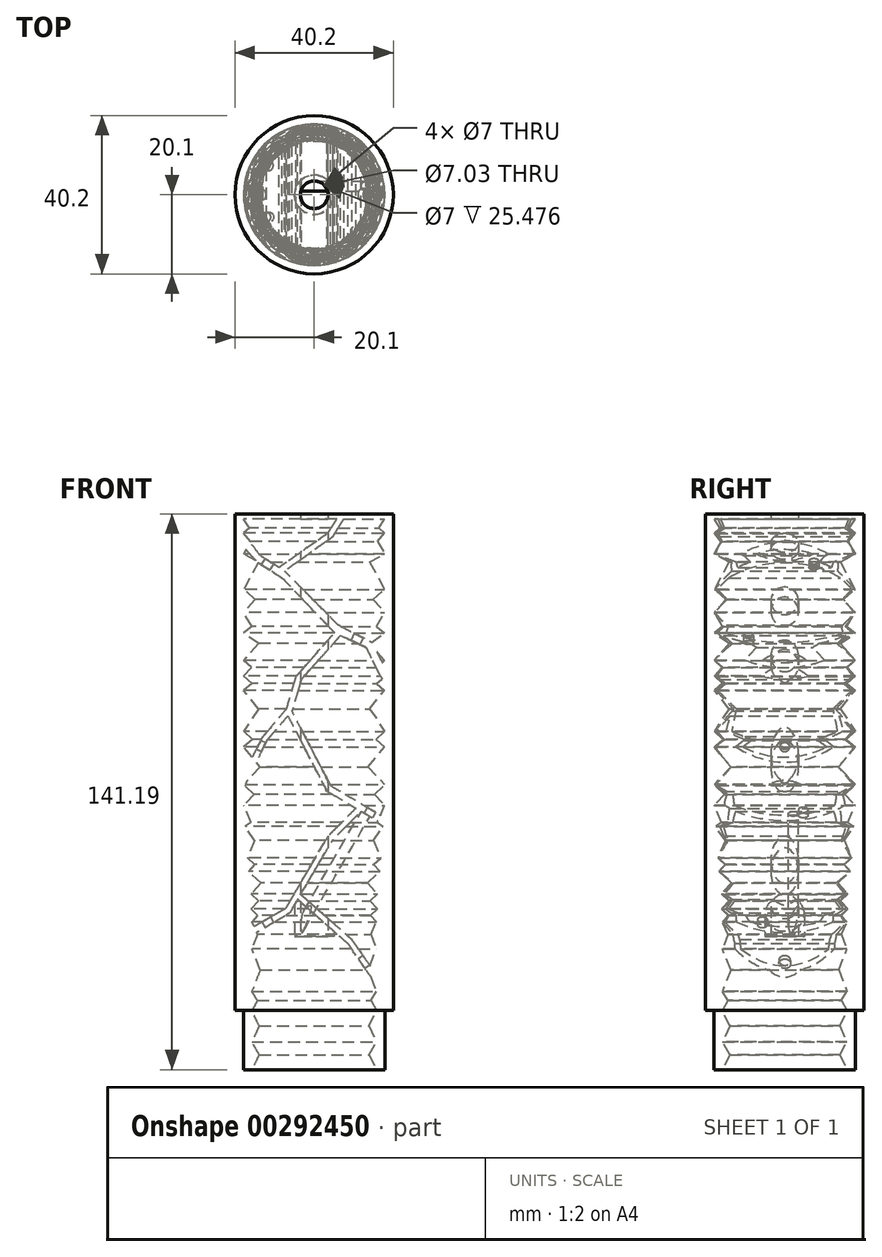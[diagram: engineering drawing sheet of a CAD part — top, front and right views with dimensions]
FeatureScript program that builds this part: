
annotation { "Feature Type Name" : "Feature", "Feature Type Description" : "" }
export const myFeature = defineFeature(function(context is Context, id is Id, definition is map)
    precondition{}
    {
        {
            var Q0;
            Q0=qCreatedBy(makeId("Front.planeOp"),FACE);
            var sketch = newSketch(context, id + "F0", { "sketchPlane" : qUnion([Q0])});
            skLineSegment(sketch, "E0", {"start": v(0, 0) * mm, "end": v(0, 175) * mm, "construction": true});
            skLineSegment(sketch, "E1", {"start": v(-3, 0) * mm, "end": v(-3, 175) * mm, "construction": true});
            skLineSegment(sketch, "E2", {"start": v(-3.5, -0.01) * mm, "end": v(-3.5, 175) * mm, "construction": true});
            skLineSegment(sketch, "E3", {"start": v(-9.9, 0) * mm, "end": v(-9.9, 175) * mm, "construction": true});
            skLineSegment(sketch, "E4", {"start": v(-20, 0) * mm, "end": v(-20, 175) * mm, "construction": true});
            skLineSegment(sketch, "E5", {"start": v(4.04, 175) * mm, "end": v(-22.22, 175) * mm, "construction": true});
            skLineSegment(sketch, "E6", {"start": v(23.08, 173.82) * mm, "end": v(-22.24, 173.82) * mm, "construction": true});
            skLineSegment(sketch, "E7", {"start": v(-17.94, 0) * mm, "end": v(-17.94, 175) * mm, "construction": true});
            skLineSegment(sketch, "E8", {"start": v(-22.12, 25) * mm, "end": v(22.75, 25) * mm, "construction": true});
            skLineSegment(sketch, "E9.MirrorCS", {"start": v(3, 0) * mm, "end": v(3, 175) * mm, "construction": true});
            skLineSegment(sketch, "E10.MirrorCS", {"start": v(17.94, 0) * mm, "end": v(17.94, 175) * mm, "construction": true});
            skLineSegment(sketch, "E11.MirrorCS", {"start": v(20, 0) * mm, "end": v(20, 175) * mm, "construction": true});
            skLineSegment(sketch, "E12.MirrorCS", {"start": v(9.9, 0) * mm, "end": v(9.9, 175) * mm, "construction": true});
            skLineSegment(sketch, "E13.MirrorCS", {"start": v(3.5, -0.01) * mm, "end": v(3.5, 175) * mm, "construction": true});
            skSolve(sketch);
        }
        {
            var Q0;
            Q0=qCreatedBy(makeId("Front.planeOp"),FACE);
            var sketch = newSketch(context, id + "F1", { "sketchPlane" : qUnion([Q0])});
            skLineSegment(sketch, "E14", {"start": v(-18.18, 170.36) * mm, "end": v(-13.69, 164.42) * mm});
            skLineSegment(sketch, "E15", {"start": v(-7.52, 160.5) * mm, "end": v(6.1, 146.8) * mm});
            skLineSegment(sketch, "E16", {"start": v(6.1, 146.8) * mm, "end": v(14.83, 142.3) * mm});
            skLineSegment(sketch, "E17", {"start": v(14.83, 142.3) * mm, "end": v(18.14, 135.62) * mm});
            skLineSegment(sketch, "E18", {"start": v(-18.18, 166.91) * mm, "end": v(-14.47, 162.75) * mm});
            skLineSegment(sketch, "E19", {"start": v(-14.47, 162.75) * mm, "end": v(-8.16, 158.78) * mm});
            skLineSegment(sketch, "E20", {"start": v(-8.16, 158.78) * mm, "end": v(5.17, 144.84) * mm});
            skLineSegment(sketch, "E21", {"start": v(13.17, 141.1) * mm, "end": v(18.14, 131.23) * mm});
            skLineSegment(sketch, "E22", {"start": v(5.17, 144.84) * mm, "end": v(-4.56, 133.73) * mm});
            skLineSegment(sketch, "E23", {"start": v(-4.56, 133.73) * mm, "end": v(-7, 125.56) * mm});
            skLineSegment(sketch, "E24", {"start": v(-7, 125.56) * mm, "end": v(-13, 118.44) * mm});
            skLineSegment(sketch, "E25", {"start": v(-13, 118.44) * mm, "end": v(-18.1, 108.79) * mm});
            skLineSegment(sketch, "E26", {"start": v(6.7, 144.13) * mm, "end": v(-3.27, 132.97) * mm});
            skLineSegment(sketch, "E27", {"start": v(-3.27, 132.97) * mm, "end": v(-5.65, 124.9) * mm});
            skLineSegment(sketch, "E28", {"start": v(-12.05, 117.46) * mm, "end": v(-18.18, 104.65) * mm});
            skLineSegment(sketch, "E29", {"start": v(-5.65, 124.9) * mm, "end": v(4.16, 105.99) * mm});
            skLineSegment(sketch, "E30", {"start": v(4.16, 105.99) * mm, "end": v(18.19, 97.67) * mm});
            skLineSegment(sketch, "E31", {"start": v(-6.67, 123.72) * mm, "end": v(3.26, 104.57) * mm});
            skLineSegment(sketch, "E32", {"start": v(11.94, 99.46) * mm, "end": v(4.73, 92.25) * mm});
            skLineSegment(sketch, "E33", {"start": v(-6.2, 73.65) * mm, "end": v(-18.06, 66.64) * mm});
            skLineSegment(sketch, "E34", {"start": v(10.6, 100.25) * mm, "end": v(3.57, 93.2) * mm});
            skLineSegment(sketch, "E35", {"start": v(3.57, 93.2) * mm, "end": v(-7.24, 74.85) * mm});
            skLineSegment(sketch, "E36", {"start": v(-7.24, 74.85) * mm, "end": v(-18.1, 68.51) * mm});
            skLineSegment(sketch, "E37", {"start": v(-7.52, 160.5) * mm, "end": v(4.81, 169.32) * mm});
            skLineSegment(sketch, "E38", {"start": v(4.81, 169.32) * mm, "end": v(7.67, 174.04) * mm});
            skLineSegment(sketch, "E39", {"start": v(-8.95, 161.41) * mm, "end": v(3.46, 170.08) * mm});
            skLineSegment(sketch, "E40", {"start": v(3.46, 170.08) * mm, "end": v(5.98, 174.08) * mm});
            skLineSegment(sketch, "E41", {"start": v(-4.19, 77.08) * mm, "end": v(8.56, 65.84) * mm});
            skLineSegment(sketch, "E42", {"start": v(8.56, 65.84) * mm, "end": v(18.14, 51.86) * mm});
            skLineSegment(sketch, "E43", {"start": v(-3.44, 78.36) * mm, "end": v(9.57, 66.88) * mm});
            skLineSegment(sketch, "E44", {"start": v(9.57, 66.88) * mm, "end": v(18.14, 54.47) * mm});
            skLineSegment(sketch, "E45", {"start": v(-13.69, 164.42) * mm, "end": v(-8.95, 161.41) * mm});
            skLineSegment(sketch, "E46", {"start": v(-18.18, 170.36) * mm, "end": v(-18.18, 166.91) * mm});
            skLineSegment(sketch, "E47", {"start": v(13.17, 141.1) * mm, "end": v(6.7, 144.13) * mm});
            skLineSegment(sketch, "E48", {"start": v(18.14, 135.62) * mm, "end": v(18.14, 131.23) * mm});
            skLineSegment(sketch, "E49", {"start": v(-12.05, 117.46) * mm, "end": v(-6.67, 123.72) * mm});
            skLineSegment(sketch, "E50", {"start": v(18.19, 97.67) * mm, "end": v(18.19, 95.85) * mm});
            skLineSegment(sketch, "E51", {"start": v(18.19, 95.85) * mm, "end": v(11.94, 99.46) * mm});
            skLineSegment(sketch, "E52", {"start": v(10.6, 100.25) * mm, "end": v(3.26, 104.57) * mm});
            skLineSegment(sketch, "E53", {"start": v(4.73, 92.25) * mm, "end": v(-3.44, 78.36) * mm});
            skLineSegment(sketch, "E54", {"start": v(-4.19, 77.08) * mm, "end": v(-6.2, 73.65) * mm});
            skLineSegment(sketch, "E55", {"start": v(-18.1, 68.51) * mm, "end": v(-18.06, 66.64) * mm});
            skLineSegment(sketch, "E56", {"start": v(18.14, 54.47) * mm, "end": v(18.14, 51.86) * mm});
            skLineSegment(sketch, "E57", {"start": v(5.98, 174.08) * mm, "end": v(7.67, 174.04) * mm});
            skLineSegment(sketch, "E58", {"start": v(-18.1, 108.79) * mm, "end": v(-18.18, 104.65) * mm});
            skSolve(sketch);
        }
        {
            var Q0;
            Q0=qSketchRegion(id+"F1",true);
            extrude(context, id + "F2", {"entities" : qUnion([Q0]), "depth" : 25 * mm, "hasSecondDirection" : true, "secondDirectionOppositeDirection" : true, "secondDirectionDepth" : 25 * mm});
        }
        {
            var Q0;
            Q0=qCreatedBy(makeId("Front.planeOp"),FACE);
            var sketch = newSketch(context, id + "F3", { "sketchPlane" : qUnion([Q0])});
            skLineSegment(sketch, "E59", {"start": v(17.93, 175.1) * mm, "end": v(17.93, -3.26) * mm});
            skLineSegment(sketch, "E60", {"start": v(17.93, -3.26) * mm, "end": v(50.8, -3.26) * mm});
            skLineSegment(sketch, "E61", {"start": v(50.8, -3.26) * mm, "end": v(50.8, 174.97) * mm});
            skLineSegment(sketch, "E62", {"start": v(50.8, 174.97) * mm, "end": v(17.93, 175.1) * mm});
            skSolve(sketch);
        }
        {
            var Q0;
            Q0=qSketchRegion(id+"F3",true);
            var Q1;
            Q1=sQuery(id+"F0.wireOp",EDGE,"E0");
            revolve(context, id + "F4", {"operationType" : NewBodyOperationType.REMOVE, "entities" : qUnion([Q0]), "axis" : qUnion([Q1]), "revolveType" : RevolveType.FULL, "oppositeDirection" : true});
        }
        {
            var Q0;
            Q0=qCreatedBy(makeId("Front.planeOp"),FACE);
            var sketch = newSketch(context, id + "F5", { "sketchPlane" : qUnion([Q0])});
            skLineSegment(sketch, "E63", {"start": v(-17.9, 173.79) * mm, "end": v(-3.52, 173.79) * mm});
            skLineSegment(sketch, "E64", {"start": v(-3.52, 173.79) * mm, "end": v(-3.52, 175) * mm});
            skLineSegment(sketch, "E65", {"start": v(-3.52, 175) * mm, "end": v(-20.1, 174.99) * mm});
            skLineSegment(sketch, "E66", {"start": v(0, 0) * mm, "end": v(0, 25.6) * mm, "construction": true});
            skLineSegment(sketch, "E67", {"start": v(-17.97, 59.66) * mm, "end": v(-17.97, 0) * mm, "construction": true});
            skLineSegment(sketch, "E68", {"start": v(-13.16, 33.82) * mm, "end": v(-23.02, 33.82) * mm, "construction": true});
            skLineSegment(sketch, "E69", {"start": v(-12.48, 48.82) * mm, "end": v(-23.12, 48.82) * mm, "construction": true});
            skLineSegment(sketch, "E70", {"start": v(-20.1, 48.82) * mm, "end": v(-17.97, 48.82) * mm});
            skLineSegment(sketch, "E71", {"start": v(-17.97, 48.82) * mm, "end": v(-17.97, 33.82) * mm});
            skLineSegment(sketch, "E72", {"start": v(-17.97, 33.82) * mm, "end": v(-15.82, 33.82) * mm});
            skLineSegment(sketch, "E73", {"start": v(-20.1, 48.82) * mm, "end": v(-20.1, 174.99) * mm});
            skLineSegment(sketch, "E74", {"start": v(-15.82, 33.82) * mm, "end": v(-13.98, 37.62) * mm});
            skLineSegment(sketch, "E75", {"start": v(-13.98, 37.62) * mm, "end": v(-15.82, 40.87) * mm});
            skLineSegment(sketch, "E76", {"start": v(-15.82, 40.87) * mm, "end": v(-13.98, 44.9) * mm});
            skLineSegment(sketch, "E77", {"start": v(-13.98, 44.9) * mm, "end": v(-15.82, 48.82) * mm});
            skLineSegment(sketch, "E78", {"start": v(-15.82, 48.82) * mm, "end": v(-14.42, 51.4) * mm});
            skLineSegment(sketch, "E79", {"start": v(-14.42, 51.4) * mm, "end": v(-15.82, 53.68) * mm});
            skLineSegment(sketch, "E80", {"start": v(-15.82, 53.68) * mm, "end": v(-13.71, 59.11) * mm});
            skLineSegment(sketch, "E81", {"start": v(-13.71, 59.11) * mm, "end": v(-15.82, 64.55) * mm});
            skLineSegment(sketch, "E82", {"start": v(-15.82, 64.55) * mm, "end": v(-14.42, 68.24) * mm});
            skLineSegment(sketch, "E83", {"start": v(-14.42, 68.24) * mm, "end": v(-15.82, 71.42) * mm});
            skLineSegment(sketch, "E84", {"start": v(-15.82, 71.42) * mm, "end": v(-14.33, 73.06) * mm});
            skLineSegment(sketch, "E85", {"start": v(-14.33, 73.06) * mm, "end": v(-16.05, 74.62) * mm});
            skLineSegment(sketch, "E86", {"start": v(-16.05, 74.62) * mm, "end": v(-14.14, 76.73) * mm});
            skLineSegment(sketch, "E87", {"start": v(-14.14, 76.73) * mm, "end": v(-16.05, 78.46) * mm});
            skLineSegment(sketch, "E88", {"start": v(-16.05, 78.46) * mm, "end": v(-13.5, 81.26) * mm});
            skLineSegment(sketch, "E89", {"start": v(-13.5, 81.26) * mm, "end": v(-16.72, 84.18) * mm});
            skLineSegment(sketch, "E90", {"start": v(-16.72, 84.18) * mm, "end": v(-15.11, 85.95) * mm});
            skLineSegment(sketch, "E91", {"start": v(-15.11, 85.95) * mm, "end": v(-16.96, 87.62) * mm});
            skLineSegment(sketch, "E92", {"start": v(-16.96, 87.62) * mm, "end": v(-15.11, 92.02) * mm});
            skLineSegment(sketch, "E93", {"start": v(-15.11, 92.02) * mm, "end": v(-17.53, 95.61) * mm});
            skLineSegment(sketch, "E94", {"start": v(-17.53, 95.61) * mm, "end": v(-16.05, 96.6) * mm});
            skLineSegment(sketch, "E95", {"start": v(-16.05, 96.6) * mm, "end": v(-17.9, 100.99) * mm});
            skLineSegment(sketch, "E96", {"start": v(-17.9, 100.99) * mm, "end": v(-15.29, 103.78) * mm});
            skLineSegment(sketch, "E97", {"start": v(-15.29, 103.78) * mm, "end": v(-17.9, 106.24) * mm});
            skLineSegment(sketch, "E98", {"start": v(-17.9, 106.24) * mm, "end": v(-13.7, 110.72) * mm});
            skLineSegment(sketch, "E99", {"start": v(-13.7, 110.72) * mm, "end": v(-17.9, 115.82) * mm});
            skLineSegment(sketch, "E100", {"start": v(-17.9, 115.82) * mm, "end": v(-15.67, 117.66) * mm});
            skLineSegment(sketch, "E101", {"start": v(-15.67, 117.66) * mm, "end": v(-17.9, 119.8) * mm});
            skLineSegment(sketch, "E102", {"start": v(-17.9, 119.8) * mm, "end": v(-14.11, 125.5) * mm});
            skLineSegment(sketch, "E103", {"start": v(-14.11, 125.5) * mm, "end": v(-17.9, 130.2) * mm});
            skLineSegment(sketch, "E104", {"start": v(-17.9, 130.2) * mm, "end": v(-15.8, 131.9) * mm});
            skLineSegment(sketch, "E105", {"start": v(-15.8, 131.9) * mm, "end": v(-17.9, 133.78) * mm});
            skLineSegment(sketch, "E106", {"start": v(-17.9, 133.78) * mm, "end": v(-15.88, 136.02) * mm});
            skLineSegment(sketch, "E107", {"start": v(-15.88, 136.02) * mm, "end": v(-17.9, 137.85) * mm});
            skLineSegment(sketch, "E108", {"start": v(-17.9, 137.85) * mm, "end": v(-14.11, 142.04) * mm});
            skLineSegment(sketch, "E109", {"start": v(-14.11, 142.04) * mm, "end": v(-17.9, 144.8) * mm});
            skLineSegment(sketch, "E110", {"start": v(-17.9, 144.8) * mm, "end": v(-15.82, 146.48) * mm});
            skLineSegment(sketch, "E111", {"start": v(-15.82, 146.48) * mm, "end": v(-17.9, 149.93) * mm});
            skLineSegment(sketch, "E112", {"start": v(-17.9, 149.93) * mm, "end": v(-14.97, 153.33) * mm});
            skLineSegment(sketch, "E113", {"start": v(-14.97, 153.33) * mm, "end": v(-17.9, 155.86) * mm});
            skLineSegment(sketch, "E114", {"start": v(-17.9, 155.86) * mm, "end": v(-14.11, 162.77) * mm});
            skLineSegment(sketch, "E115", {"start": v(-14.11, 162.77) * mm, "end": v(-17.9, 164.85) * mm});
            skLineSegment(sketch, "E116", {"start": v(-17.9, 164.85) * mm, "end": v(-16.15, 168.05) * mm});
            skLineSegment(sketch, "E117", {"start": v(-16.15, 168.05) * mm, "end": v(-17.9, 170.23) * mm});
            skLineSegment(sketch, "E118", {"start": v(-17.9, 170.23) * mm, "end": v(-16.44, 171.41) * mm});
            skLineSegment(sketch, "E119", {"start": v(-16.44, 171.41) * mm, "end": v(-17.9, 173.79) * mm});
            skSolve(sketch);
        }
        {
            var Q0;
            Q0=qSketchRegion(id+"F5",true);
            var Q1;
            Q1=sQuery(id+"F5.wireOp",EDGE,"E66");
            revolve(context, id + "F6", {"operationType" : NewBodyOperationType.ADD, "entities" : qUnion([Q0]), "axis" : qUnion([Q1]), "revolveType" : RevolveType.FULL});
        }
        {
            var Q0;
            Q0=qCreatedBy(makeId("Top.planeOp"),FACE);
            var sketch = newSketch(context, id + "F7", { "sketchPlane" : qUnion([Q0])});
            skCircle(sketch, "E120", {"center": v(0, 0) * mm, "radius": 3.5 * mm});
            skSolve(sketch);
        }
        {
            var Q0;
            Q0=qSketchRegion(id+"F7",true);
            extrude(context, id + "F8", {"entities" : qUnion([Q0]), "operationType" : NewBodyOperationType.REMOVE, "endBound" : BoundingType.THROUGH_ALL, "depth" : 25 * mm});
        }
        {
            var Q0;
            Q0=qCreatedBy(makeId("Top.planeOp"),FACE);
            cPlane(context, id + "F9", {"entities" : qUnion([Q0]), "cplaneType" : CPlaneType.OFFSET, "offset" : 67.7 * mm, "width" : 150 * mm, "height" : 150 * mm});
        }
        {
            var Q0;
            Q0=qCreatedBy(id+"F9.planeOp",FACE);
            var sketch = newSketch(context, id + "F10", { "sketchPlane" : qUnion([Q0])});
            skCircle(sketch, "E121", {"center": v(0, 0) * mm, "radius": 3.5 * mm});
            skCircle(sketch, "E122", {"center": v(0, 0) * mm, "radius": 5 * mm});
            skSolve(sketch);
        }
        {
            var Q0;
            Q0=qSketchRegion(id+"F10",true);
            var Q1;
            Q1=makeQuery(id+"F2.opExtrude","SWEPT_FACE",FACE,{"disambiguationData":[OSD([sQuery(id+"F1.wireOp",EDGE,"E41")])]});
            extrude(context, id + "F11", {"entities" : qUnion([Q0]), "operationType" : NewBodyOperationType.ADD, "endBound" : BoundingType.UP_TO_SURFACE, "endBoundEntityFace" : qUnion([Q1]), "depth" : 25 * mm});
        }
        {
            var Q0;
            Q0=makeQuery(id+"F2.opExtrude","SWEPT_FACE",FACE,{"disambiguationData":[OSD([sQuery(id+"F1.wireOp",EDGE,"E42")])]});
            var sketch = newSketch(context, id + "F12", { "sketchPlane" : qUnion([Q0])});
            skCircle(sketch, "E123", {"center": v(0, 43.27) * mm, "radius": 1.5 * mm});
            skSolve(sketch);
        }
        {
            var Q0;
            Q0 = qSketchRegion(id + "F12", true);
            extrude(context, id + "F13", {"entities" : qUnion([Q0]), "operationType" : NewBodyOperationType.REMOVE, "endBound" : BoundingType.UP_TO_NEXT, "oppositeDirection" : true, "depth" : 25 * mm});
        }
        {
            var Q0;
            Q0=makeQuery(id+"F2.opExtrude","SWEPT_FACE",FACE,{"disambiguationData":[OSD([sQuery(id+"F1.wireOp",EDGE,"E33")])]});
            var sketch = newSketch(context, id + "F14", { "sketchPlane" : qUnion([Q0])});
            skCircle(sketch, "E124", {"center": v(26.13, 5.67) * mm, "radius": 1.25 * mm});
            skSolve(sketch);
        }
        {
            var Q0;
            Q0 = qSketchRegion(id + "F14", true);
            extrude(context, id + "F15", {"entities" : qUnion([Q0]), "operationType" : NewBodyOperationType.REMOVE, "endBound" : BoundingType.UP_TO_NEXT, "oppositeDirection" : true, "depth" : 25 * mm});
        }
        {
            var Q0;
            Q0=makeQuery(id+"F2.opExtrude","SWEPT_FACE",FACE,{"disambiguationData":[OSD([sQuery(id+"F1.wireOp",EDGE,"E51")])]});
            var sketch = newSketch(context, id + "F16", { "sketchPlane" : qUnion([Q0])});
            skCircle(sketch, "E125", {"center": v(-38.18, -2.19) * mm, "radius": 1.25 * mm});
            skSolve(sketch);
        }
        {
            var Q0;
            {var subQ0=sQuery(id+"F1.wireOp",EDGE,"E51");Q0=makeQuery(id+"F16.imprint","IMPRINT",FACE,{"disambiguationData":[TD([[makeQuery(id+"F16.imprint","IMPRINT",EDGE,{"derivedFrom":makeQuery(id+"F2.opExtrude","SWEPT_EDGE",EDGE,{"disambiguationData":[OSD([sQuery(id+"F1.wireOp",EDGE,"E32"),subQ0])]})}),1.0]])]});}
            var sketch = newSketch(context, id + "F17", { "sketchPlane" : qUnion([Q0])});
            skCircle(sketch, "E126", {"center": v(-37.39, -4.7) * mm, "radius": 1.25 * mm});
            skSolve(sketch);
        }
        {
            var Q0;
            Q0 = qSketchRegion(id + "F17", true);
            extrude(context, id + "F18", {"entities" : qUnion([Q0]), "operationType" : NewBodyOperationType.REMOVE, "endBound" : BoundingType.UP_TO_NEXT, "oppositeDirection" : true, "depth" : 25 * mm});
        }
        {
            var Q0;
            Q0=makeQuery(id+"F2.opExtrude","SWEPT_FACE",FACE,{"disambiguationData":[OSD([sQuery(id+"F1.wireOp",EDGE,"E28")])]});
            var sketch = newSketch(context, id + "F19", { "sketchPlane" : qUnion([Q0])});
            skCircle(sketch, "E127", {"center": v(0, 98.9) * mm, "radius": 1.25 * mm});
            skSolve(sketch);
        }
        {
            var Q0;
            Q0 = qSketchRegion(id + "F19", true);
            extrude(context, id + "F20", {"entities" : qUnion([Q0]), "operationType" : NewBodyOperationType.REMOVE, "endBound" : BoundingType.UP_TO_NEXT, "oppositeDirection" : true, "depth" : 25 * mm, "hasSecondDirection" : true, "secondDirectionOppositeDirection" : false, "secondDirectionDepth" : 25 * mm});
        }
        {
            var Q0;
            Q0=makeQuery(id+"F2.opExtrude","SWEPT_FACE",FACE,{"disambiguationData":[OSD([sQuery(id+"F1.wireOp",EDGE,"E47")])]});
            var sketch = newSketch(context, id + "F21", { "sketchPlane" : qUnion([Q0])});
            skCircle(sketch, "E128", {"center": v(-50.8, 9.25) * mm, "radius": 1.25 * mm});
            skSolve(sketch);
        }
        {
            var Q0;
            Q0 = qSketchRegion(id + "F21", true);
            extrude(context, id + "F22", {"entities" : qUnion([Q0]), "operationType" : NewBodyOperationType.REMOVE, "endBound" : BoundingType.UP_TO_NEXT, "oppositeDirection" : true, "depth" : 25 * mm});
        }
        {
            var Q0;
            Q0=makeQuery(id+"F2.opExtrude","SWEPT_FACE",FACE,{"disambiguationData":[OSD([sQuery(id+"F1.wireOp",EDGE,"E19")])]});
            var sketch = newSketch(context, id + "F23", { "sketchPlane" : qUnion([Q0])});
            skCircle(sketch, "E129", {"center": v(-96.44, -7.43) * mm, "radius": 1.25 * mm});
            skSolve(sketch);
        }
        {
            var Q0;
            Q0 = qSketchRegion(id + "F23", true);
            extrude(context, id + "F24", {"entities" : qUnion([Q0]), "operationType" : NewBodyOperationType.REMOVE, "endBound" : BoundingType.UP_TO_NEXT, "oppositeDirection" : true, "depth" : 25 * mm});
        }
        {
            var Q0;
            Q0 = qSketchRegion(id + "F16", true);
            extrude(context, id + "F25", {"entities" : qUnion([Q0]), "operationType" : NewBodyOperationType.ADD, "endBound" : BoundingType.UP_TO_NEXT, "depth" : 25 * mm});
        }
    });
